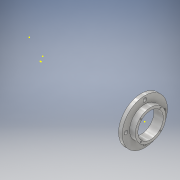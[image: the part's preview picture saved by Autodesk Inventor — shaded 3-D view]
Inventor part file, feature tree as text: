
AUTODESK INVENTOR PART (.ipt)
format: ipt  version: 2017.3 (Build 213256000, 256)  size: 252,416 bytes
history: native  units: mm
features: sketch x28, plane x21, extrude x13, other x8, hole x7, move_body x2
ambient origin geometry x8: Origin, YZ Plane, XZ Plane, XY Plane, X Axis, Y Axis, Z Axis, Center Point
bodies: Solid1 (feature_tree)
feature tree (79):
  extrude  "Extrusion1"  Depth=100.0mm TaperAngle=0.0deg
  sketch  "Sketch5"  dims[d13=-5.0mm d14=0.0mm d15=0.0mm d16=10.0mm d17=0.0mm d18=0.0mm]
  move_body  "Move Body1"
  move_body  "Move Body2"
  extrude  "Extrusion4"  Depth=10.0mm TaperAngle=0.0deg
  extrude  "Extrusion6"  Depth=5.0mm TaperAngle=0.0deg
  extrude  "Extrusion7"  Depth=95.0mm TaperAngle=0.0deg
  plane  "Work Plane4"
  plane  "Work Plane5"
  plane  "Work Plane11"
  extrude  "Extrusion8"  [1 undecoded]
  hole  "Hole8"  [1 undecoded]
  other  "Work Axis7"
  other  "Work Axis8"
  other  "Work Axis9"
  other  "Work Axis10"
  other  "Work Axis11"
  other  "Work Axis12"
  other  "Work Axis13"
  plane  "Work Plane27"
  plane  "Work Plane28"
  plane  "Work Plane29"
  plane  "Work Plane30"
  plane  "Work Plane31"
  plane  "Work Plane32"
  plane  "Work Plane33"
  plane  "Work Plane34"
  sketch  "Sketch27"  dims[d97=1.67mm d98=1.67mm]
  sketch  "Sketch28"  dims[d99=1.67mm d100=1.67mm]
  sketch  "Sketch29"  dims[d101=4.0mm d102=0.0mm]
  plane  "Work Plane35"
  plane  "Work Plane36"
  plane  "Work Plane37"
  plane  "Work Plane38"
  sketch  "Sketch30"  dims[d103=1.221mm d104=2.0mm d105=4.0mm d106=2.0mm d107=90.0deg d108=2.0mm d109=20.594885mm d110=-9.295mm d111=9.295mm d112=-9.295mm d113=9.295mm]
  sketch  "Sketch31"  dims[d114=9.295mm d115=-9.295mm]
  sketch  "Sketch32"  dims[d116=1.221mm d117=3.2mm d118=4.0mm d119=2.0mm d120=90.0deg d121=5.39mm d122=20.594885mm]
  sketch  "Sketch33"  dims[d123=1.221mm d124=3.2mm d125=4.0mm d126=2.0mm d127=90.0deg d128=5.39mm d129=20.594885mm]
  hole  "Hole9"  [1 undecoded]
  hole  "Hole10"  [1 undecoded]
  hole  "Hole12"  [1 undecoded]
  hole  "Hole13"  [1 undecoded]
  hole  "Hole14"  [1 undecoded]
  plane  "Work Plane42"
  plane  "Work Plane43"
  plane  "Work Plane44"
  sketch  "Sketch35"  dims[d137=1.221mm d138=3.2mm d139=4.0mm d140=2.0mm d141=90.0deg d142=5.39mm d143=20.594885mm]
  sketch  "Sketch39"  dims[d144=1.221mm d145=3.2mm d146=4.0mm d147=2.0mm d148=90.0deg d149=5.39mm d150=20.594885mm]
  extrude  "Extrusion9"  Depth=4.0mm TaperAngle=0.0deg
  hole  "Hole20"  [1 undecoded]
  extrude  "Extrusion11"  Depth=5.0mm TaperAngle=0.0deg
  extrude  "Extrusion12"  Depth=4.0mm TaperAngle=0.0deg
  extrude  "Extrusion13"  Depth=39.1mm
  extrude  "Extrusion14"  Depth=3.175mm
  sketch  "Sketch49"  dims[d222=95.0mm d223=0.0mm d232=39.1mm]
  sketch  "Sketch50"  dims[d233=3.175mm d234=0.0mm d235=22.0mm]
  sketch  "Sketch51"  dims[d236=3.175mm d237=0.0mm d238=3.175mm]
  extrude  "Extrusion15"  Depth=3.175mm
  extrude  "Extrusion16"  Depth=3.175mm
  sketch  "Sketch54"  dims[d199=1.0mm]
  extrude  "Extrusion17"  Depth=3.175mm TaperAngle=0.0deg
  sketch  "Sketch1"  dims[d0=26.4mm d1=100.0mm d2=0.0mm]
  sketch  "Sketch6"  dims[d21=1.0mm d22=5.0mm d23=0.0mm]
  sketch  "Sketch8"  dims[d35=22.0mm d36=95.0mm d37=0.0mm]
  sketch  "Sketch25"  dims[d38=90.0mm d39=0.0mm d47=-13.2mm]
  sketch  "Sketch26"  dims[d55=0.0mm d96=1.67mm]
  other  "Work Axis14"
  plane  "Work Plane39"
  plane  "Work Plane40"
  plane  "Work Plane41"
  sketch  "Sketch40"  dims[d151=1.221mm d152=3.2mm d153=4.0mm d154=2.0mm d155=90.0deg d156=5.39mm d157=20.594885mm d158=-2.617994mm]
  sketch  "Sketch44"  dims[d159=1.1mm d160=-26.4mm d161=90.0deg d162=13.2mm d163=-13.2mm]
  sketch  "Sketch45"  dims[d192=1.6mm d193=4.0mm d194=0.0mm]
  sketch  "Sketch46"  dims[d206=1.567mm d207=4.0mm d208=4.0mm d209=2.0mm d210=90.0deg d211=2.0mm d212=20.594885mm d213=1.6mm]
  sketch  "Sketch47"  dims[d214=5.0mm d215=0.0mm d217=4.0mm d218=0.0mm]
  sketch  "Sketch48"  dims[d219=1.67mm d220=4.0mm d221=0.0mm]
  sketch  "Sketch52"  dims[d239=3.175mm d240=3.175mm]
  sketch  "Sketch53"  dims[d241=3.175mm d242=3.175mm d243=0.0mm]
  sketch  "Sketch55"  dims[d200=1.0mm]
note: 8 required parameter values undecoded (feature->parameter linkage not recoverable at this tier; creation-order binding heuristic only, values carry confidence <= 0.55)
